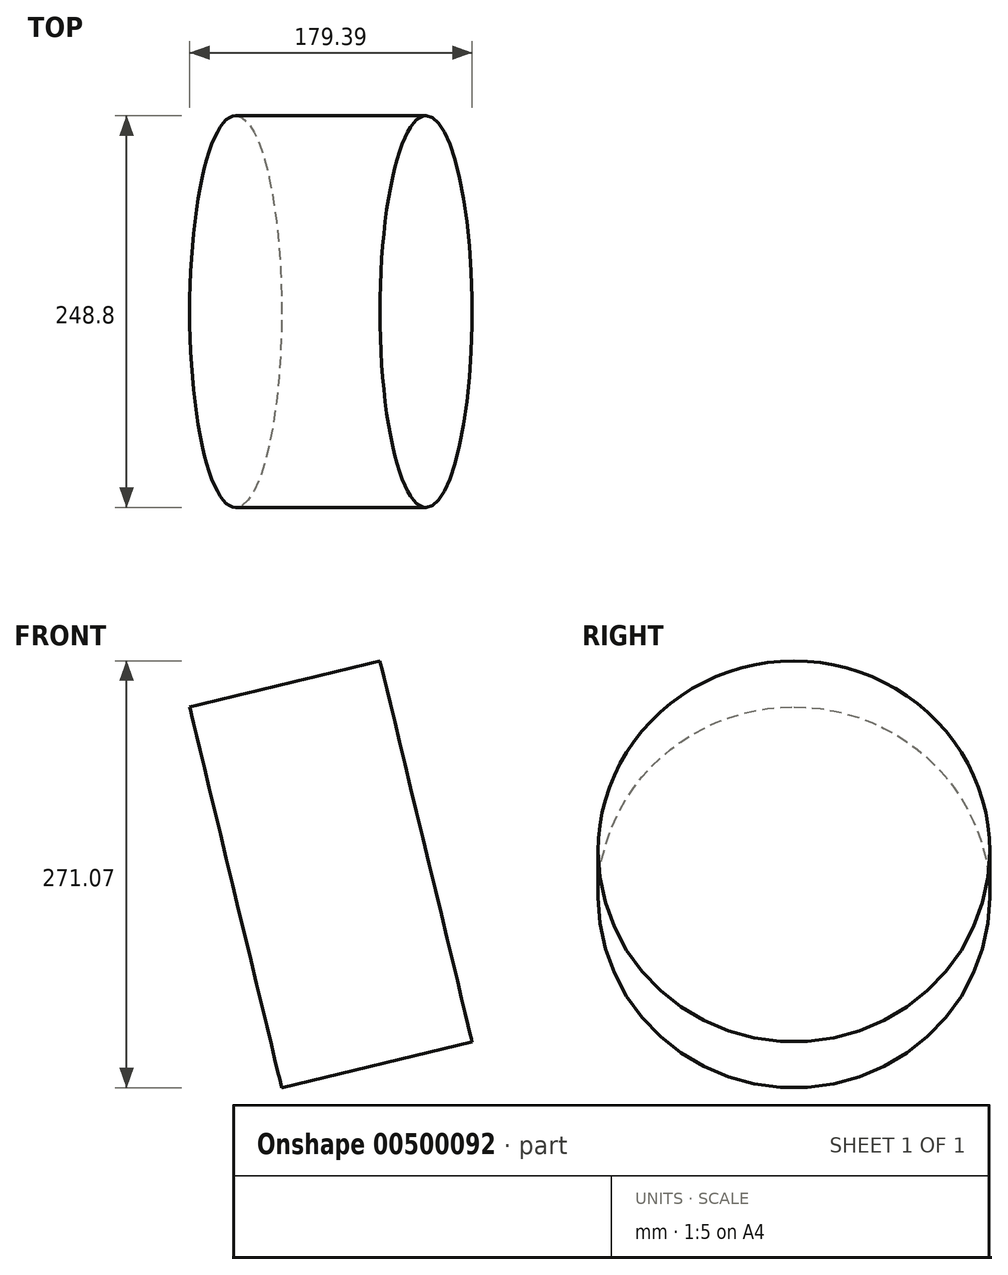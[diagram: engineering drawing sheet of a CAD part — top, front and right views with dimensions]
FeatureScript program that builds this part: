
annotation { "Feature Type Name" : "Feature", "Feature Type Description" : "" }
export const myFeature = defineFeature(function(context is Context, id is Id, definition is map)
    precondition{}
    {
        {
            var Q0;
            Q0=qCreatedBy(makeId("Front.planeOp"),FACE);
            var sketch = newSketch(context, id + "F0", { "sketchPlane" : qUnion([Q0])});
            skCircle(sketch, "E0.cCircle", {"center": v(0, 0) * mm, "radius": 87.97 * mm, "construction": true});
            skLineSegment(sketch, "E0.0", {"start": v(-75.08, 45.84) * mm, "end": v(45.84, 75.08) * mm});
            skLineSegment(sketch, "E0.1", {"start": v(45.84, 75.08) * mm, "end": v(75.08, -45.84) * mm});
            skLineSegment(sketch, "E0.2", {"start": v(75.08, -45.84) * mm, "end": v(-45.84, -75.08) * mm});
            skLineSegment(sketch, "E0.3", {"start": v(-45.84, -75.08) * mm, "end": v(-75.08, 45.84) * mm});
            skSolve(sketch);
        }
        {
            var Q0;
            Q0=makeQuery(id+"F0.imprint","IMPRINT",FACE,{"disambiguationData":[TD([[makeQuery(id+"F0.imprint","IMPRINT",EDGE,{"derivedFrom":sQuery(id+"F0.wireOp",EDGE,"E0.0")}),-1.0]])]});
            var Q1;
            Q1=sQuery(id+"F0.wireOp",EDGE,"E0.0");
            revolve(context, id + "F1", {"entities" : qUnion([Q0]), "axis" : qUnion([Q1]), "revolveType" : RevolveType.FULL});
        }
    });
